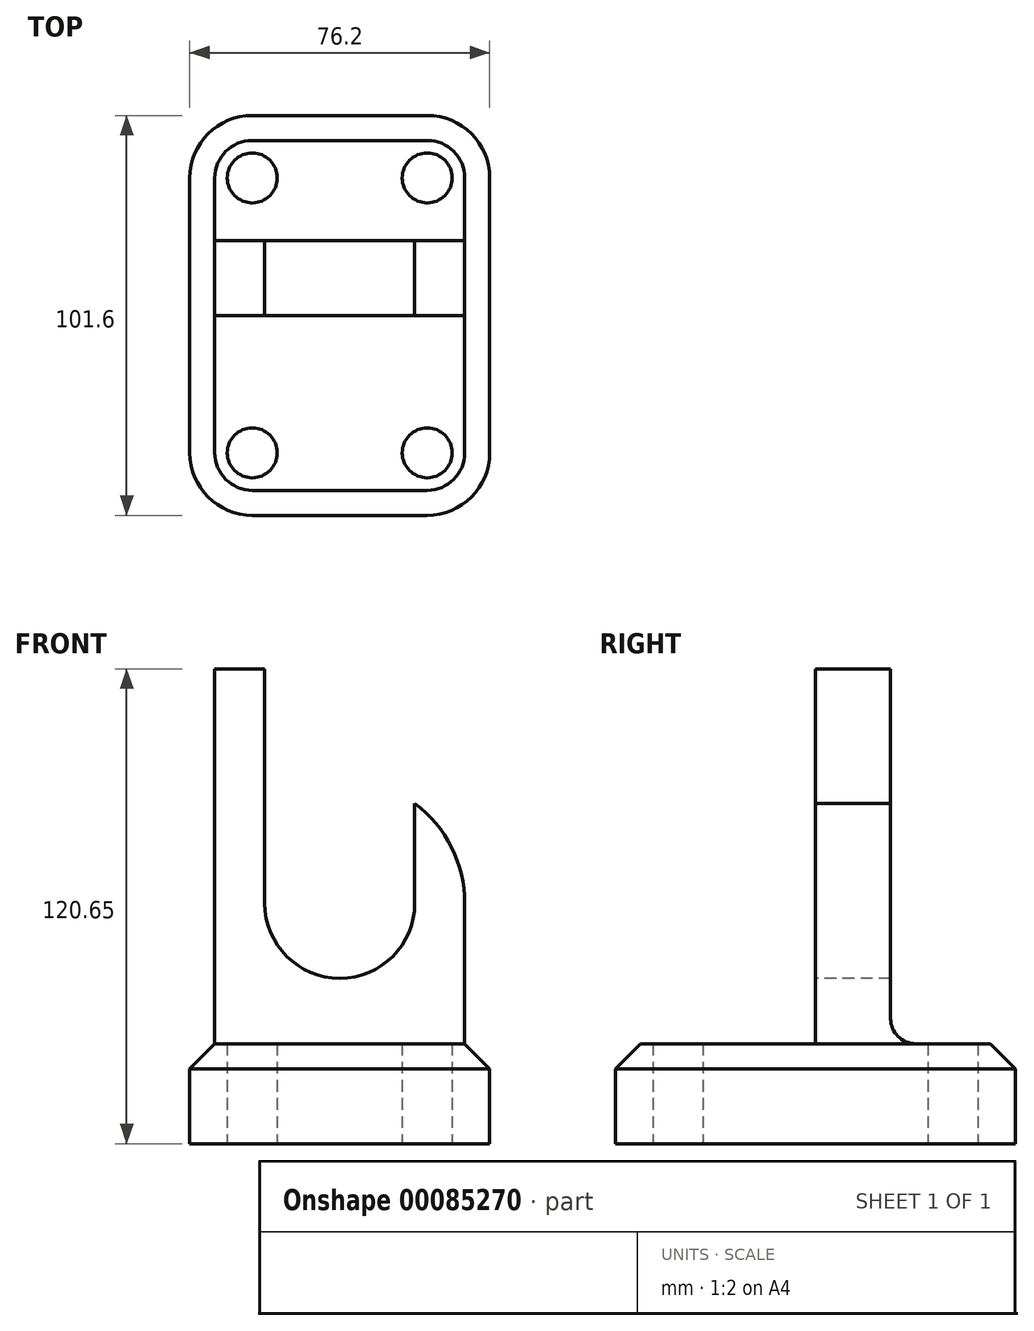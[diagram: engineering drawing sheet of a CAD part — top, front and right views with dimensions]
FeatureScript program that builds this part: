
annotation { "Feature Type Name" : "Feature", "Feature Type Description" : "" }
export const myFeature = defineFeature(function(context is Context, id is Id, definition is map)
    precondition{}
    {
        {
            var Q0;
            Q0=qCreatedBy(makeId("Top.planeOp"),FACE);
            var sketch = newSketch(context, id + "F0", { "sketchPlane" : qUnion([Q0])});
            skLineSegment(sketch, "E0.bottom", {"start": v(15.87, 0) * mm, "end": v(60.33, 0) * mm});
            skLineSegment(sketch, "E0.top", {"start": v(15.88, 101.6) * mm, "end": v(60.32, 101.6) * mm});
            skLineSegment(sketch, "E0.left", {"start": v(0, 15.87) * mm, "end": v(0, 85.73) * mm});
            skLineSegment(sketch, "E0.right", {"start": v(76.2, 15.88) * mm, "end": v(76.2, 85.73) * mm});
            skPoint(sketch, "E1.visualSharp", {"position": v(0, 0) * mm});
            skArc(sketch, "E1.filletArc", {"start": v(0, 15.87) * mm, "mid": v(4.65, 4.65) * mm, "end": v(15.87, 0) * mm});
            skPoint(sketch, "E2.visualSharp", {"position": v(76.2, 0) * mm});
            skArc(sketch, "E2.filletArc", {"start": v(60.33, 0) * mm, "mid": v(71.55, 4.65) * mm, "end": v(76.2, 15.88) * mm});
            skPoint(sketch, "E3.visualSharp", {"position": v(76.2, 101.6) * mm});
            skArc(sketch, "E3.filletArc", {"start": v(76.2, 85.73) * mm, "mid": v(71.55, 96.95) * mm, "end": v(60.32, 101.6) * mm});
            skPoint(sketch, "E4.visualSharp", {"position": v(0, 101.6) * mm});
            skArc(sketch, "E4.filletArc", {"start": v(15.88, 101.6) * mm, "mid": v(4.65, 96.95) * mm, "end": v(0, 85.73) * mm});
            skCircle(sketch, "E5", {"center": v(15.87, 15.88) * mm, "radius": 6.35 * mm});
            skCircle(sketch, "E6", {"center": v(60.33, 15.88) * mm, "radius": 6.35 * mm});
            skCircle(sketch, "E7", {"center": v(60.32, 85.73) * mm, "radius": 6.35 * mm});
            skCircle(sketch, "E8", {"center": v(15.88, 85.73) * mm, "radius": 6.35 * mm});
            skSolve(sketch);
        }
        {
            var Q0;
            Q0=makeQuery(id+"F0.imprint","IMPRINT",FACE,{"disambiguationData":[TD([[makeQuery(id+"F0.imprint","IMPRINT",EDGE,{"derivedFrom":sQuery(id+"F0.wireOp",EDGE,"E0.bottom")}),1.0]])]});
            extrude(context, id + "F1", {"entities" : qUnion([Q0]), "depth" : 25.4 * mm});
        }
        {
            var Q0;
            Q0=makeQuery(id+"F1.opExtrude","CAP_EDGE",EDGE,{"disambiguationData":[OSD([sQuery(id+"F0.wireOp",EDGE,"E0.bottom")])],"isStart":false});
            chamfer(context, id + "F2", {"entities" : qUnion([Q0]), "width" : 6.35 * mm, "tangentPropagation" : true});
        }
        {
            var Q0;
            Q0=makeQuery(id+"F1.opExtrude","CAP_FACE",FACE,{"disambiguationData":[OSD([sQuery(id+"F0.wireOp",EDGE,"E0.bottom"),sQuery(id+"F0.wireOp",EDGE,"E0.top"),sQuery(id+"F0.wireOp",EDGE,"E0.left"),sQuery(id+"F0.wireOp",EDGE,"E0.right"),sQuery(id+"F0.wireOp",EDGE,"E1.filletArc"),sQuery(id+"F0.wireOp",EDGE,"E2.filletArc"),sQuery(id+"F0.wireOp",EDGE,"E3.filletArc"),sQuery(id+"F0.wireOp",EDGE,"E4.filletArc"),sQuery(id+"F0.wireOp",EDGE,"E5"),sQuery(id+"F0.wireOp",EDGE,"E6"),sQuery(id+"F0.wireOp",EDGE,"E7"),sQuery(id+"F0.wireOp",EDGE,"E8")])],"isStart":false});
            var sketch = newSketch(context, id + "F3", { "sketchPlane" : qUnion([Q0])});
            skLineSegment(sketch, "E9.bottom", {"start": v(0, 0) * mm, "end": v(6.35, 0) * mm});
            skLineSegment(sketch, "E9.top", {"start": v(0, 50.8) * mm, "end": v(6.35, 50.8) * mm});
            skLineSegment(sketch, "E9.left", {"start": v(0, 0) * mm, "end": v(0, 50.8) * mm});
            skLineSegment(sketch, "E9.right", {"start": v(6.35, 0) * mm, "end": v(6.35, 50.8) * mm});
            skLineSegment(sketch, "E10.bottom", {"start": v(6.35, 50.8) * mm, "end": v(69.85, 50.8) * mm});
            skLineSegment(sketch, "E10.top", {"start": v(6.35, 69.85) * mm, "end": v(69.85, 69.85) * mm});
            skLineSegment(sketch, "E10.left", {"start": v(6.35, 50.8) * mm, "end": v(6.35, 69.85) * mm});
            skLineSegment(sketch, "E10.right", {"start": v(69.85, 50.8) * mm, "end": v(69.85, 69.85) * mm});
            skSolve(sketch);
        }
        {
            var Q0;
            Q0=makeQuery(id+"F3.imprint","IMPRINT",FACE,{"disambiguationData":[TD([[makeQuery(id+"F3.imprint","IMPRINT",EDGE,{"derivedFrom":sQuery(id+"F3.wireOp",EDGE,"E10.bottom")}),1.0]])]});
            extrude(context, id + "F4", {"entities" : qUnion([Q0]), "operationType" : NewBodyOperationType.ADD, "depth" : 95.25 * mm});
        }
        {
            var Q0;
            Q0=makeQuery(id+"F4.opExtrude","CAP_EDGE",EDGE,{"disambiguationData":[OSD([sQuery(id+"F3.wireOp",EDGE,"E10.bottom")])],"isStart":true});
            var Q1;
            Q1=makeQuery(id+"F4.opExtrude","CAP_EDGE",EDGE,{"disambiguationData":[OSD([sQuery(id+"F3.wireOp",EDGE,"E10.top")])],"isStart":true});
            fillet(context, id + "F5", {"entities" : qUnion([Q0, Q1]), "radius" : 6.35 * mm, "tangentPropagation" : true, "allowEdgeOverflow" : false});
        }
        {
            var Q0;
            Q0=makeQuery(id+"F4.opExtrude","SWEPT_FACE",FACE,{"disambiguationData":[OSD([sQuery(id+"F3.wireOp",EDGE,"E10.bottom")])]});
            var sketch = newSketch(context, id + "F6", { "sketchPlane" : qUnion([Q0])});
            skPoint(sketch, "E11.oppositeSnap0", {"position": v(38.1, 120.65) * mm});
            skLineSegment(sketch, "E11.bottom", {"start": v(0, -2.42) * mm, "end": v(38.1, -2.42) * mm});
            skLineSegment(sketch, "E11.top", {"start": v(0, 61.08) * mm, "end": v(38.1, 61.08) * mm});
            skLineSegment(sketch, "E11.left", {"start": v(0, -2.42) * mm, "end": v(0, 61.08) * mm});
            skLineSegment(sketch, "E11.right", {"start": v(38.1, -2.42) * mm, "end": v(38.1, 61.08) * mm});
            skCircle(sketch, "E12", {"center": v(38.1, 61.08) * mm, "radius": 31.75 * mm});
            skCircle(sketch, "E13", {"center": v(38.1, 61.08) * mm, "radius": 19.05 * mm});
            skLineSegment(sketch, "E14", {"start": v(19.05, 61.08) * mm, "end": v(19.05, 120.65) * mm});
            skLineSegment(sketch, "E15", {"start": v(19.05, 120.65) * mm, "end": v(19.05, 61.08) * mm});
            skLineSegment(sketch, "E16", {"start": v(57.15, 61.08) * mm, "end": v(57.15, 120.65) * mm});
            skLineSegment(sketch, "E17", {"start": v(57.15, 120.65) * mm, "end": v(19.05, 120.65) * mm});
            skSolve(sketch);
        }
        {
            var Q0;
            {var subQ0=sQuery(id+"F6.wireOp",EDGE,"E15");var subQ1=sQuery(id+"F6.wireOp",EDGE,"E12");var subQ2=makeQuery(id+"F6.imprint","INTERSECT",VERTEX,{"derivedFrom":[subQ1,subQ0]});Q0=makeQuery(id+"F6.imprint","IMPRINT",FACE,{"disambiguationData":[TD([[makeQuery(id+"F6.imprint","IMPRINT",EDGE,{"disambiguationData":[TD([[subQ2,1.0]])],"derivedFrom":subQ0}),-1.0]])]});}
            var Q1;
            {var subQ5=sQuery(id+"F6.wireOp",EDGE,"E17");Q1=makeQuery(id+"F6.imprint","IMPRINT",FACE,{"disambiguationData":[TD([[makeQuery(id+"F6.imprint","IMPRINT",EDGE,{"derivedFrom":subQ5}),-1.0]])]});}
            var Q2;
            {var subQ0=sQuery(id+"F6.wireOp",EDGE,"E16");var subQ1=sQuery(id+"F6.wireOp",EDGE,"E12");var subQ2=makeQuery(id+"F6.imprint","INTERSECT",VERTEX,{"derivedFrom":[subQ1,subQ0]});Q2=makeQuery(id+"F6.imprint","IMPRINT",FACE,{"disambiguationData":[TD([[makeQuery(id+"F6.imprint","IMPRINT",EDGE,{"disambiguationData":[TD([[subQ2,-1.0]])],"derivedFrom":subQ0}),-1.0]])]});}
            var Q3;
            {var subQ0=sQuery(id+"F6.wireOp",EDGE,"E16");var subQ1=sQuery(id+"F6.wireOp",EDGE,"E12");var subQ2=makeQuery(id+"F6.imprint","INTERSECT",VERTEX,{"derivedFrom":[subQ1,subQ0]});Q3=makeQuery(id+"F6.imprint","IMPRINT",FACE,{"disambiguationData":[TD([[makeQuery(id+"F6.imprint","IMPRINT",EDGE,{"disambiguationData":[TD([[subQ2,-1.0]])],"derivedFrom":subQ1}),1.0]])]});}
            var Q4;
            {var subQ0=sQuery(id+"F6.wireOp",EDGE,"E11.right");var subQ1=sQuery(id+"F6.wireOp",EDGE,"E11.top");var subQ2=makeQuery(id+"F6.imprint","INTERSECT",VERTEX,{"derivedFrom":[subQ1,subQ0]});Q4=makeQuery(id+"F6.imprint","IMPRINT",FACE,{"disambiguationData":[TD([[makeQuery(id+"F6.imprint","IMPRINT",EDGE,{"disambiguationData":[TD([[subQ2,1.0]])],"derivedFrom":subQ0}),-1.0]])]});}
            var Q5;
            {var subQ0=sQuery(id+"F6.wireOp",EDGE,"E11.right");var subQ1=sQuery(id+"F6.wireOp",EDGE,"E11.top");var subQ2=makeQuery(id+"F6.imprint","INTERSECT",VERTEX,{"derivedFrom":[subQ1,subQ0]});Q5=makeQuery(id+"F6.imprint","IMPRINT",FACE,{"disambiguationData":[TD([[makeQuery(id+"F6.imprint","IMPRINT",EDGE,{"disambiguationData":[TD([[subQ2,1.0]])],"derivedFrom":subQ0}),1.0]])]});}
            extrude(context, id + "F7", {"entities" : qUnion([Q0, Q1, Q2, Q3, Q4, Q5]), "operationType" : NewBodyOperationType.REMOVE, "endBound" : BoundingType.THROUGH_ALL, "oppositeDirection" : true, "depth" : 25.4 * mm});
        }
    });
